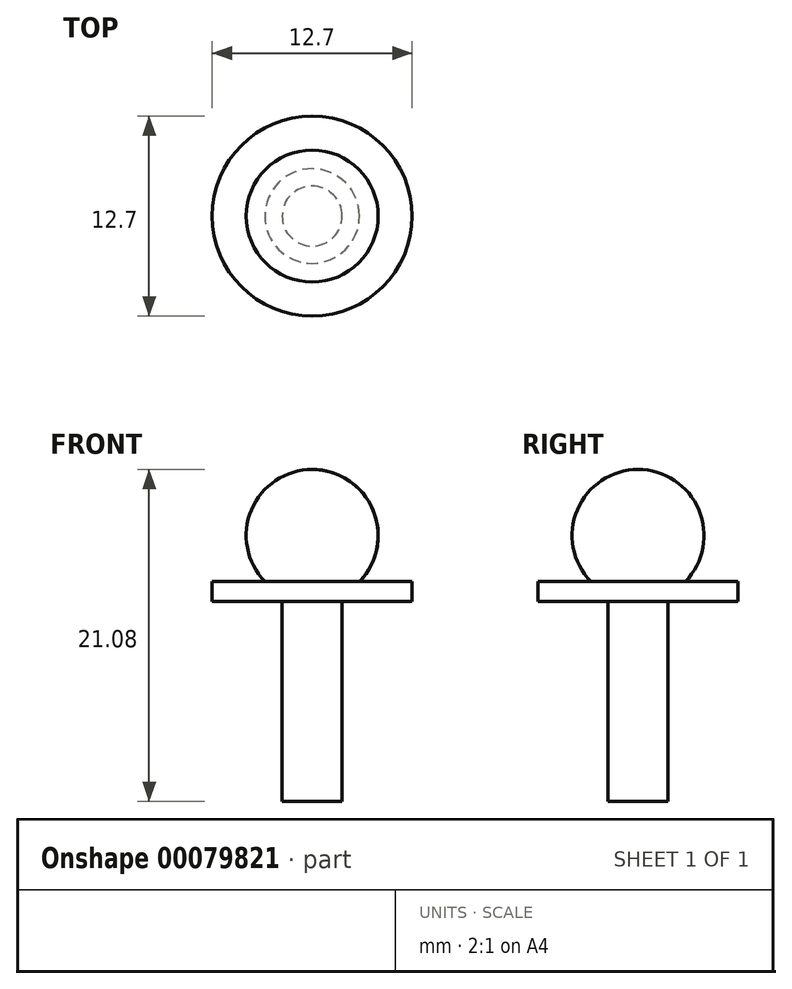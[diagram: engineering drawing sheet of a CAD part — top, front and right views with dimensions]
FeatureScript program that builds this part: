
annotation { "Feature Type Name" : "Feature", "Feature Type Description" : "" }
export const myFeature = defineFeature(function(context is Context, id is Id, definition is map)
    precondition{}
    {
        {
            var Q0;
            Q0=qCreatedBy(makeId("Top.planeOp"),FACE);
            var sketch = newSketch(context, id + "F0", { "sketchPlane" : qUnion([Q0])});
            skCircle(sketch, "E0", {"center": v(0, 0) * mm, "radius": 4.2 * mm});
            skSolve(sketch);
        }
        {
            var Q0;
            Q0=qSketchRegion(id+"F0",true);
            extrude(context, id + "F1", {"entities" : qUnion([Q0]), "depth" : 73.66 * mm});
        }
        {
            var Q0;
            Q0=makeQuery(id+"F1.opExtrude","CAP_FACE",FACE,{"disambiguationData":[OSD([sQuery(id+"F0.wireOp",EDGE,"E0")])],"isStart":false});
            var sketch = newSketch(context, id + "F2", { "sketchPlane" : qUnion([Q0])});
            skCircle(sketch, "E1", {"center": v(0, 0) * mm, "radius": 4.2 * mm});
            skSolve(sketch);
        }
        {
            var Q0;
            Q0=qSketchRegion(id+"F2",true);
            extrude(context, id + "F3", {"entities" : qUnion([Q0]), "depth" : 8.38 * mm});
        }
        {
            var Q0;
            Q0=makeQuery(id+"F3.opExtrude","CAP_EDGE",EDGE,{"disambiguationData":[OSD([sQuery(id+"F2.wireOp",EDGE,"E1")])],"isStart":true});
            var Q1;
            Q1=makeQuery(id+"F3.opExtrude","CAP_EDGE",EDGE,{"disambiguationData":[OSD([sQuery(id+"F2.wireOp",EDGE,"E1")])],"isStart":false});
            fillet(context, id + "F4", {"entities" : qUnion([Q0, Q1]), "radius" : 4.2 * mm, "tangentPropagation" : true, "allowEdgeOverflow" : false});
        }
        {
            var Q0;
            Q0=makeQuery(id+"F1.opExtrude","CAP_FACE",FACE,{"disambiguationData":[OSD([sQuery(id+"F0.wireOp",EDGE,"E0")])],"isStart":false});
            var sketch = newSketch(context, id + "F5", { "sketchPlane" : qUnion([Q0])});
            skCircle(sketch, "E2", {"center": v(0, 0) * mm, "radius": 6.35 * mm});
            skSolve(sketch);
        }
        {
            var Q0;
            Q0=qSketchRegion(id+"F5",true);
            extrude(context, id + "F6", {"entities" : qUnion([Q0]), "operationType" : NewBodyOperationType.ADD, "depth" : 1.27 * mm});
        }
        {
            var Q0;
            Q0=makeQuery(id+"F1.opExtrude","CAP_FACE",FACE,{"disambiguationData":[OSD([sQuery(id+"F0.wireOp",EDGE,"E0")])],"isStart":true});
            var sketch = newSketch(context, id + "F7", { "sketchPlane" : qUnion([Q0])});
            skCircle(sketch, "E3", {"center": v(0, 0) * mm, "radius": 29.9 * mm});
            skSolve(sketch);
        }
        {
            var Q0;
            Q0 = qSketchRegion(id + "F7", true);
            extrude(context, id + "F8", {"entities" : qUnion([Q0]), "operationType" : NewBodyOperationType.REMOVE, "oppositeDirection" : true, "depth" : 73.66 * mm});
        }
        {
            var Q0;
            Q0=makeQuery(id+"F8.boolean.opBoolean","MERGE",FACE,{"derivedFrom":[makeQuery(id+"F6.opExtrude","CAP_FACE",FACE,{"disambiguationData":[OSD([sQuery(id+"F5.wireOp",EDGE,"E2")])],"isStart":true}),makeQuery(id+"F8.opExtrude","CAP_FACE",FACE,{"disambiguationData":[OSD([sQuery(id+"F7.wireOp",EDGE,"E3")])],"isStart":false})]});
            var sketch = newSketch(context, id + "F9", { "sketchPlane" : qUnion([Q0])});
            skCircle(sketch, "E4", {"center": v(0, 0) * mm, "radius": 1.9 * mm});
            skSolve(sketch);
        }
        {
            var Q0;
            Q0 = qSketchRegion(id + "F9", true);
            extrude(context, id + "F10", {"entities" : qUnion([Q0]), "operationType" : NewBodyOperationType.ADD, "depth" : 12.7 * mm});
        }
    });
